# Revit family: Accessory-Tumbler-KOHLER-STILLNESS-K-14463T-1
name_source: partatom
category: Specialty Equipment
units: mm (PartAtom-declared; Revit-internal decimal feet)

## family parameters
Cut with Voids When Loaded = No
Host = Face
OmniClass Number = 23.31.25.00
OmniClass Title = Toilet and Bath Specialties
Part Type = Normal
Room Calculation Point = No
Round Connector Dimension = Use Diameter
Shared = No

## types (6) — shared parameters
ADA Compliant = No
Assembly Code = C1030200
Date Modified = 05/17/2024
Default Elevation = 42"
Description = Stighetti gargle cup holder
Height = 1 7/8"
Length = 5 1/16"
Manufacturer = Kohler Co.
Master Format 2014 = 10 28 00
Master Format 2014 Name = Toilet, Bath, and Laundry Accessories
Material = Premium Material Constraction
Product Documentation Link = https://files.kohler.com.cn
Product Name = STILLNESS
URL = http://www.kohler.com.cn
WaterSense Certified = No
Width = 1 7/8"

## per-type parameters (varying)
| type | Finish | Model | Product Page URL | Type |
| CP-Polished Chrome | Kohler-Metal-CP-Polished_Chrome | K-14463T-CP | https://www.kohler.com.cn | 1 |
| SN-Vibrant Polished Nickel | Kohler-Metal-SN-Vibrant_Polished_Nickel | K-14463T-SN | https://www.kohler.com.cn | 2 |
| BN-Vibrant Brushed Nickel | Kohler-Metal-BN-Vibrant_Brushed_Nickel | K-14463T-BN | https://www.kohler.com.cn | 3 |
| PGD-Modern Polished Gold | Kohler-Metal-PGD-Modern_Polished_Gold | K-14463T-PGD | https://www.kohler.com.cn | 4 |
| RGD-Polished Rose Gold | Kohler-Metal-RGD-Polished_Rose_Gold | K-14463T-RGD | https://www.kohler.com.cn | 5 |
| AF-Vibrant French Gold | Kohler-Metal-AF-Vibrant_French_Gold | K-14463T-AF |  | 6 |

## geometry (parser evidence)
native form markers: Sweep x5
no freeform markers — native parametric forms only
